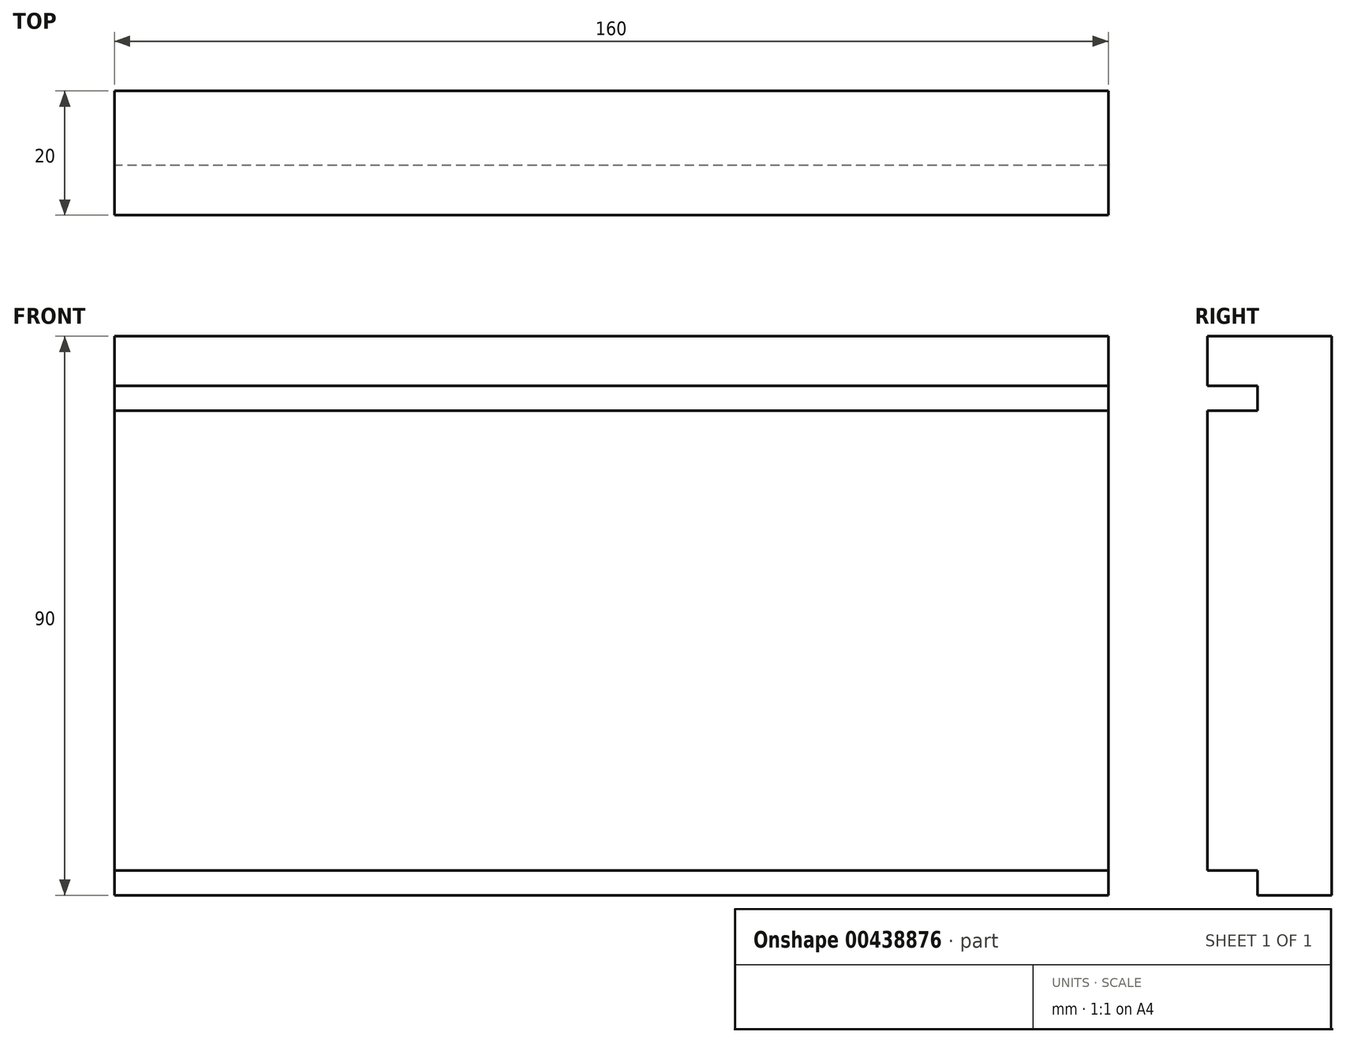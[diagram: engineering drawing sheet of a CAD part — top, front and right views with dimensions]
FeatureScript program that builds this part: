
annotation { "Feature Type Name" : "Feature", "Feature Type Description" : "" }
export const myFeature = defineFeature(function(context is Context, id is Id, definition is map)
    precondition{}
    {
        {
            var Q0;
            Q0=qCreatedBy(makeId("Right.planeOp"),FACE);
            var sketch = newSketch(context, id + "F0", { "sketchPlane" : qUnion([Q0])});
            skLineSegment(sketch, "E0.bottom", {"start": v(-9.1, 37.6) * mm, "end": v(10.9, 37.6) * mm});
            skLineSegment(sketch, "E0.top", {"start": v(-1.1, -52.4) * mm, "end": v(10.9, -52.4) * mm});
            skLineSegment(sketch, "E0.left", {"start": v(-9.1, 37.6) * mm, "end": v(-9.1, 29.6) * mm});
            skLineSegment(sketch, "E0.right", {"start": v(10.9, 37.6) * mm, "end": v(10.9, -52.4) * mm});
            skLineSegment(sketch, "E1.top", {"start": v(-9.1, -48.4) * mm, "end": v(-1.1, -48.4) * mm});
            skLineSegment(sketch, "E1.right", {"start": v(-1.1, -52.4) * mm, "end": v(-1.1, -48.4) * mm});
            skLineSegment(sketch, "E2.bottom", {"start": v(-9.1, 29.6) * mm, "end": v(-1.1, 29.6) * mm});
            skLineSegment(sketch, "E2.top", {"start": v(-9.1, 25.6) * mm, "end": v(-1.1, 25.6) * mm});
            skLineSegment(sketch, "E2.right", {"start": v(-1.1, 29.6) * mm, "end": v(-1.1, 25.6) * mm});
            skLineSegment(sketch, "E3.trimOffspring", {"start": v(-9.1, 25.6) * mm, "end": v(-9.1, -48.4) * mm});
            skSolve(sketch);
        }
        {
            var Q0;
            Q0=makeQuery(id+"F0.imprint","IMPRINT",FACE,{"disambiguationData":[TD([[makeQuery(id+"F0.imprint","IMPRINT",EDGE,{"derivedFrom":sQuery(id+"F0.wireOp",EDGE,"E0.bottom")}),-1.0]])]});
            extrude(context, id + "F1", {"entities" : qUnion([Q0]), "depth" : 160 * mm});
        }
    });
